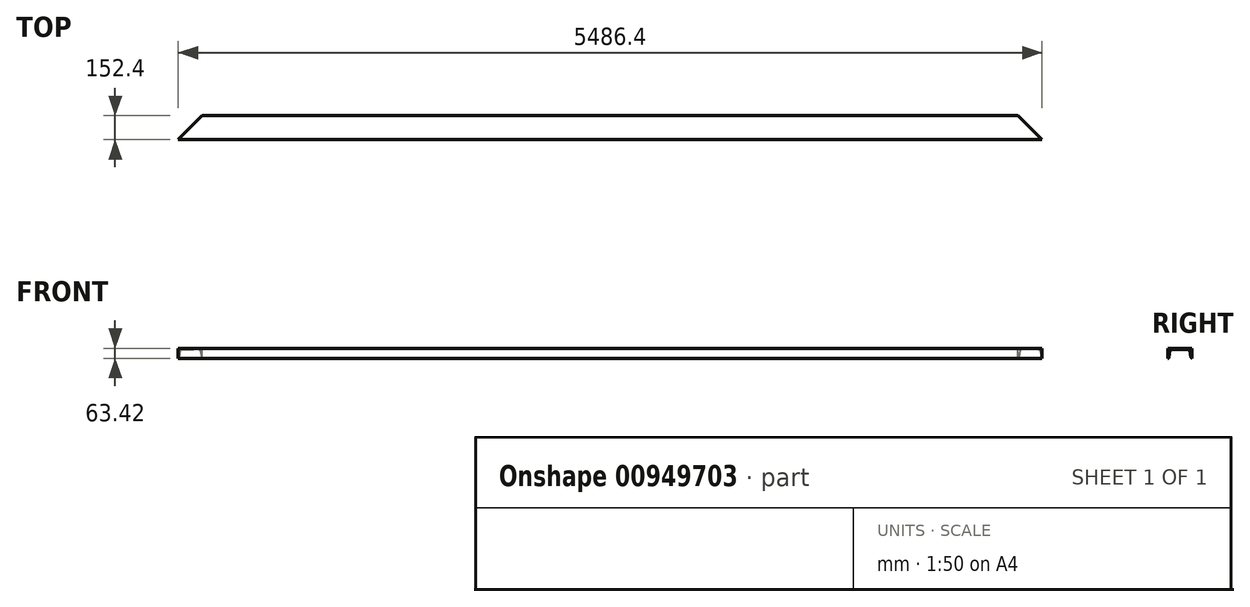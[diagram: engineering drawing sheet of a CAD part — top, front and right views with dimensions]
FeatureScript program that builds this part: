
annotation { "Feature Type Name" : "Feature", "Feature Type Description" : "" }
export const myFeature = defineFeature(function(context is Context, id is Id, definition is map)
    precondition{}
    {
        {
            var Q0;
            Q0=qCreatedBy(makeId("Right.planeOp"),FACE);
            var sketch = newSketch(context, id + "F0", { "sketchPlane" : qUnion([Q0])});
            skLineSegment(sketch, "E0", {"start": v(-76.2, 0) * mm, "end": v(76.2, 0) * mm});
            skLineSegment(sketch, "E1", {"start": v(76.2, 0) * mm, "end": v(76.2, -63.42) * mm});
            skLineSegment(sketch, "E2", {"start": v(-76.2, 0) * mm, "end": v(-76.2, -63.42) * mm});
            skLineSegment(sketch, "E3", {"start": v(-63.12, -15.57) * mm, "end": v(-70.65, -58.76) * mm});
            skLineSegment(sketch, "E4", {"start": v(63.12, -15.57) * mm, "end": v(70.65, -58.76) * mm});
            skLineSegment(sketch, "E5", {"start": v(-53.98, -7.87) * mm, "end": v(53.98, -7.87) * mm});
            skArc(sketch, "E6.filletArc", {"start": v(-76.2, -63.42) * mm, "mid": v(-72.57, -62.1) * mm, "end": v(-70.65, -58.76) * mm});
            skArc(sketch, "E7.filletArc", {"start": v(70.65, -58.76) * mm, "mid": v(72.57, -62.1) * mm, "end": v(76.2, -63.42) * mm});
            skArc(sketch, "E8.filletArc", {"start": v(-53.98, -7.87) * mm, "mid": v(-59.95, -10.05) * mm, "end": v(-63.12, -15.57) * mm});
            skArc(sketch, "E9.filletArc", {"start": v(63.12, -15.57) * mm, "mid": v(59.95, -10.05) * mm, "end": v(53.98, -7.87) * mm});
            skSolve(sketch);
        }
        {
            var Q0;
            Q0 = qSketchRegion(id + "F0", true);
            extrude(context, id + "F1", {"entities" : qUnion([Q0]), "depth" : 5486.4 * mm, "offsetDistance" : 25.4 * mm});
        }
        {
            var Q0;
            Q0=makeQuery(id+"F1.opExtrude","SWEPT_FACE",FACE,{"disambiguationData":[OSD([sQuery(id+"F0.wireOp",EDGE,"E0")])]});
            var sketch = newSketch(context, id + "F2", { "sketchPlane" : qUnion([Q0])});
            skLineSegment(sketch, "E10", {"start": v(0, -76.2) * mm, "end": v(152.4, 76.2) * mm});
            skLineSegment(sketch, "E11", {"start": v(152.4, 76.2) * mm, "end": v(0, 76.2) * mm});
            skLineSegment(sketch, "E12", {"start": v(0, 76.2) * mm, "end": v(0, -76.2) * mm});
            skLineSegment(sketch, "E13", {"start": v(5486.4, -76.2) * mm, "end": v(5334, 76.2) * mm});
            skLineSegment(sketch, "E14", {"start": v(5334, 76.2) * mm, "end": v(5486.4, 76.2) * mm});
            skLineSegment(sketch, "E15", {"start": v(5486.4, 76.2) * mm, "end": v(5486.4, -76.2) * mm});
            skSolve(sketch);
        }
        {
            var Q0;
            Q0 = qSketchRegion(id + "F2", true);
            extrude(context, id + "F3", {"entities" : qUnion([Q0]), "operationType" : NewBodyOperationType.REMOVE, "endBound" : BoundingType.THROUGH_ALL, "oppositeDirection" : true, "depth" : 25.4 * mm, "offsetDistance" : 25.4 * mm});
        }
    });
